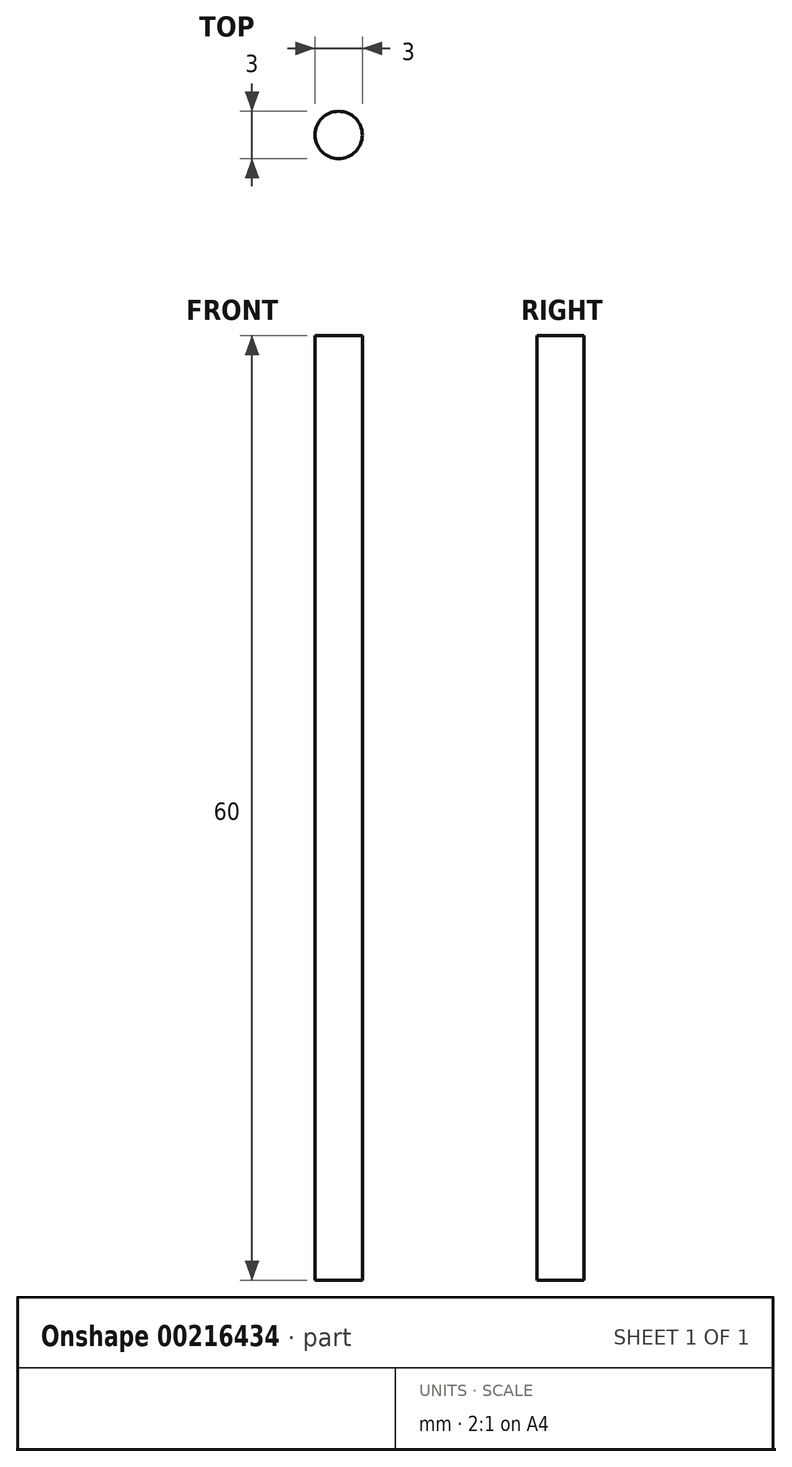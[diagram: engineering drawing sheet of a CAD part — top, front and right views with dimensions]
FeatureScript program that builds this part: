
annotation { "Feature Type Name" : "Feature", "Feature Type Description" : "" }
export const myFeature = defineFeature(function(context is Context, id is Id, definition is map)
    precondition{}
    {
        {
            var Q0;
            Q0=qCreatedBy(makeId("Top.planeOp"),FACE);
            var sketch = newSketch(context, id + "F0", { "sketchPlane" : qUnion([Q0])});
            skCircle(sketch, "E0", {"center": v(0, 0) * mm, "radius": 1.5 * mm});
            skSolve(sketch);
        }
        {
            var Q0;
            Q0 = qSketchRegion(id + "F0", true);
            extrude(context, id + "F1", {"entities" : qUnion([Q0]), "endBound" : BoundingType.SYMMETRIC, "depth" : 60 * mm});
        }
    });
